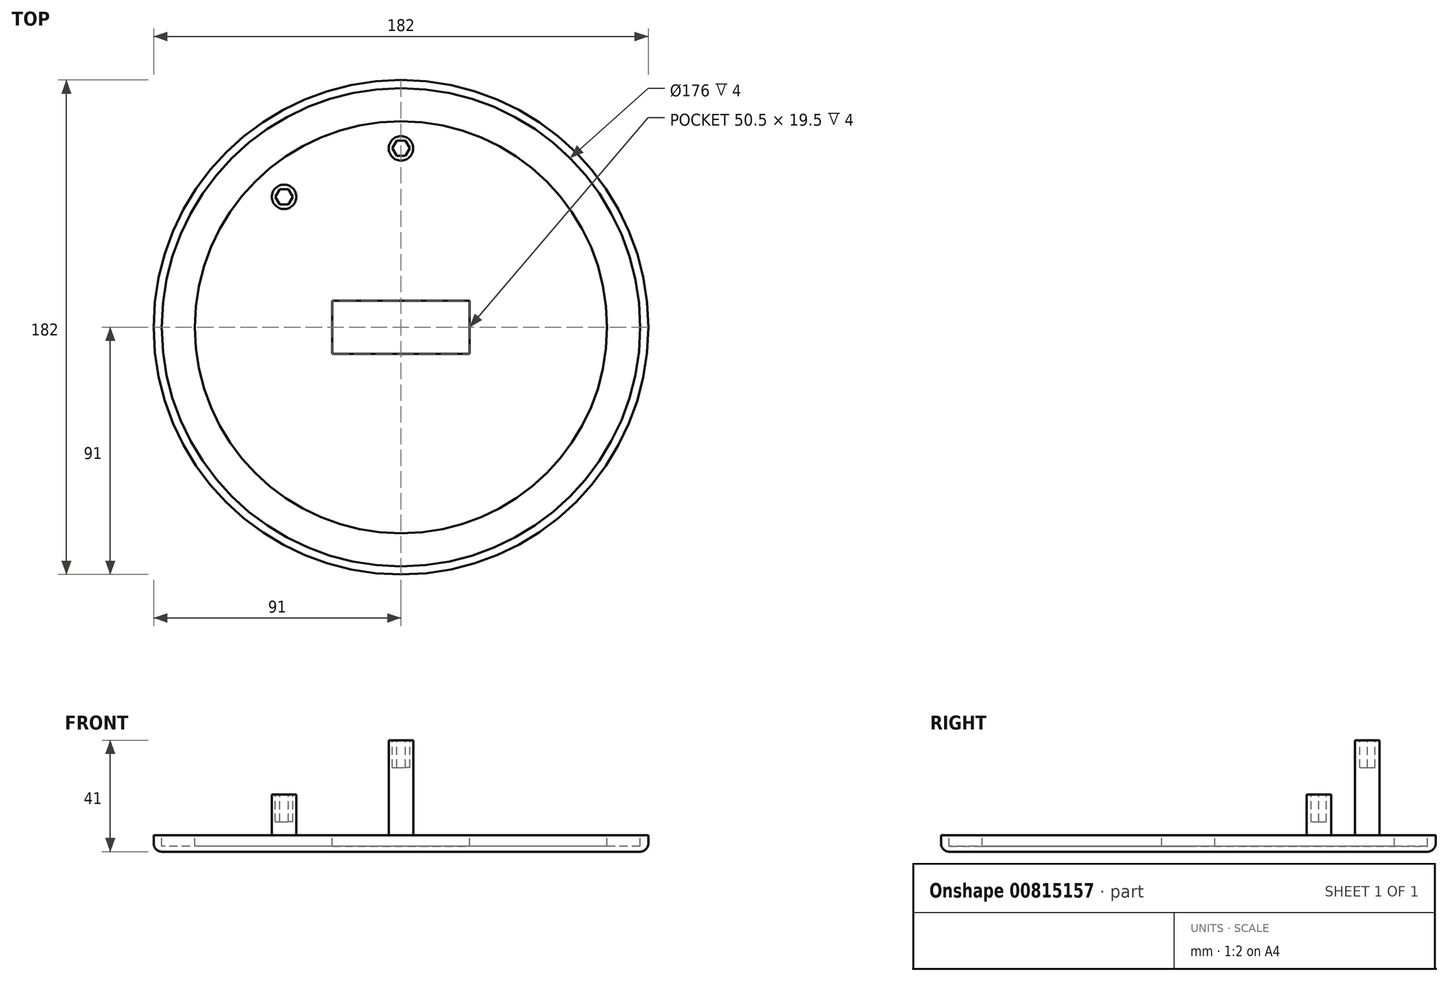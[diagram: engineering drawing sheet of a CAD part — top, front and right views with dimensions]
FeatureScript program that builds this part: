
annotation { "Feature Type Name" : "Feature", "Feature Type Description" : "" }
export const myFeature = defineFeature(function(context is Context, id is Id, definition is map)
    precondition{}
    {
        {
            var Q0;
            Q0=qCreatedBy(makeId("Top.planeOp"),FACE);
            var sketch = newSketch(context, id + "F0", { "sketchPlane" : qUnion([Q0])});
            skCircle(sketch, "E0", {"center": v(0, 0) * mm, "radius": 91 * mm});
            skSolve(sketch);
        }
        {
            var Q0;
            Q0=makeQuery(id+"F0.imprint","IMPRINT",FACE,{"disambiguationData":[TD([[makeQuery(id+"F0.imprint","IMPRINT",EDGE,{"derivedFrom":sQuery(id+"F0.wireOp",EDGE,"E0")}),1.0]])]});
            var Q1;
            Q1=sQuery(id+"F0.wireOp",EDGE,"E0");
            extrude(context, id + "F1", {"entities" : qUnion([Q0]), "surfaceEntities" : qUnion([Q1]), "depth" : 6 * mm, "offsetDistance" : 25 * mm});
        }
        {
            var Q0;
            Q0=makeQuery(id+"F1.opExtrude","CAP_FACE",FACE,{"disambiguationData":[OSD([sQuery(id+"F0.wireOp",EDGE,"E0")])],"isStart":false});
            var sketch = newSketch(context, id + "F2", { "sketchPlane" : qUnion([Q0])});
            skCircle(sketch, "E1", {"center": v(0, 0) * mm, "radius": 88 * mm});
            skSolve(sketch);
        }
        {
            var Q0;
            Q0=makeQuery(id+"F2.imprint","IMPRINT",FACE,{"disambiguationData":[TD([[makeQuery(id+"F2.imprint","IMPRINT",EDGE,{"derivedFrom":sQuery(id+"F2.wireOp",EDGE,"E1")}),-1.0]])]});
            var sketch = newSketch(context, id + "F3", { "sketchPlane" : qUnion([Q0])});
            skCircle(sketch, "E2", {"center": v(0, 0) * mm, "radius": 75.85 * mm});
            skSolve(sketch);
        }
        {
            var Q0;
            Q0=makeQuery(id+"F3.imprint","IMPRINT",FACE,{"disambiguationData":[TD([[makeQuery(id+"F3.imprint","IMPRINT",EDGE,{"derivedFrom":sQuery(id+"F3.wireOp",EDGE,"E2")}),-1.0]])]});
            var Q1;
            Q1=sQuery(id+"F2.wireOp",EDGE,"E1");
            var Q2;
            Q2=sQuery(id+"F3.wireOp",EDGE,"E2");
            extrude(context, id + "F4", {"entities" : qUnion([Q0]), "operationType" : NewBodyOperationType.REMOVE, "surfaceEntities" : qUnion([Q1, Q2]), "oppositeDirection" : true, "depth" : 4 * mm, "offsetDistance" : 25 * mm});
        }
        {
            var Q0;
            Q0=makeQuery(id+"F4.boolean.opBoolean","SPLIT",FACE,{"disambiguationData":[TD([makeQuery(id+"F4.opExtrude","SWEPT_FACE",FACE,{"disambiguationData":[OSD([sQuery(id+"F3.wireOp",EDGE,"E2")])]})])],"derivedFrom":makeQuery(id+"F1.opExtrude","CAP_FACE",FACE,{"disambiguationData":[OSD([sQuery(id+"F0.wireOp",EDGE,"E0")])],"isStart":false})});
            var sketch = newSketch(context, id + "F5", { "sketchPlane" : qUnion([Q0])});
            skLineSegment(sketch, "E3.bottom", {"start": v(-25.25, 9.75) * mm, "end": v(25.25, 9.75) * mm});
            skLineSegment(sketch, "E3.top", {"start": v(-25.25, -9.75) * mm, "end": v(25.25, -9.75) * mm});
            skLineSegment(sketch, "E3.left", {"start": v(-25.25, 9.75) * mm, "end": v(-25.25, -9.75) * mm});
            skLineSegment(sketch, "E3.right", {"start": v(25.25, 9.75) * mm, "end": v(25.25, -9.75) * mm});
            skPoint(sketch, "E3.middle", {"position": v(0, 0) * mm});
            skSolve(sketch);
        }
        {
            var Q0;
            Q0=qSketchRegion(id+"F5",true);
            extrude(context, id + "F6", {"entities" : qUnion([Q0]), "operationType" : NewBodyOperationType.REMOVE, "oppositeDirection" : true, "depth" : 4 * mm, "offsetDistance" : 25 * mm});
        }
        {
            var Q0;
            Q0=makeQuery(id+"FstaHTkGCtETjQ8_1.boolean.opBoolean","SPLIT",FACE,{"disambiguationData":[TD([makeQuery(id+"F6.boolean.opBoolean","COPY",FACE,{"derivedFrom":makeQuery(id+"F6.opExtrude","SWEPT_FACE",FACE,{"disambiguationData":[OSD([sQuery(id+"F5.wireOp",EDGE,"E3.bottom")])]})})])],"derivedFrom":makeQuery(id+"F4.boolean.opBoolean","SPLIT",FACE,{"disambiguationData":[TD([makeQuery(id+"F4.opExtrude","SWEPT_FACE",FACE,{"disambiguationData":[OSD([sQuery(id+"F3.wireOp",EDGE,"E2")])]})])],"derivedFrom":makeQuery(id+"F1.opExtrude","CAP_FACE",FACE,{"disambiguationData":[OSD([sQuery(id+"F0.wireOp",EDGE,"E0")])],"isStart":false})})});
            var sketch = newSketch(context, id + "F7", { "sketchPlane" : qUnion([Q0])});
            skLineSegment(sketch, "E4.bottom", {"start": v(-48, 53) * mm, "end": v(48, 53) * mm});
            skLineSegment(sketch, "E4.top", {"start": v(-48, -53) * mm, "end": v(48, -53) * mm});
            skLineSegment(sketch, "E4.left", {"start": v(-48, 53) * mm, "end": v(-48, -53) * mm});
            skLineSegment(sketch, "E4.right", {"start": v(48, 53) * mm, "end": v(48, -53) * mm});
            skPoint(sketch, "E4.middle", {"position": v(0, 0) * mm});
            skSolve(sketch);
        }
        {
            var Q0;
            Q0=makeQuery(id+"F7.imprint","IMPRINT",FACE,{"disambiguationData":[TD([[makeQuery(id+"F7.imprint","IMPRINT",EDGE,{"derivedFrom":sQuery(id+"F7.wireOp",EDGE,"E4.bottom")}),1.0]])]});
            var sketch = newSketch(context, id + "F8", { "sketchPlane" : qUnion([Q0])});
            skCircle(sketch, "E5", {"center": v(0, 65.85) * mm, "radius": 4.5 * mm});
            skSolve(sketch);
        }
        {
            var Q0;
            Q0=qSketchRegion(id+"F8",true);
            extrude(context, id + "F9", {"entities" : qUnion([Q0]), "operationType" : NewBodyOperationType.ADD, "depth" : 35 * mm, "offsetDistance" : 25 * mm});
        }
        {
            var Q0;
            Q0=makeQuery(id+"F9.opExtrude","CAP_FACE",FACE,{"disambiguationData":[OSD([sQuery(id+"F8.wireOp",EDGE,"E5")])],"isStart":false});
            var sketch = newSketch(context, id + "F10", { "sketchPlane" : qUnion([Q0])});
            skCircle(sketch, "E6.cCircle", {"center": v(0, 65.85) * mm, "radius": 3.23 * mm, "construction": true});
            skLineSegment(sketch, "E6.0", {"start": v(-1.62, 68.65) * mm, "end": v(1.62, 68.65) * mm});
            skLineSegment(sketch, "E6.1", {"start": v(1.62, 68.65) * mm, "end": v(3.23, 65.85) * mm});
            skLineSegment(sketch, "E6.2", {"start": v(3.23, 65.85) * mm, "end": v(1.62, 63.05) * mm});
            skLineSegment(sketch, "E6.3", {"start": v(1.62, 63.05) * mm, "end": v(-1.62, 63.05) * mm});
            skLineSegment(sketch, "E6.4", {"start": v(-1.62, 63.05) * mm, "end": v(-3.23, 65.85) * mm});
            skLineSegment(sketch, "E6.5", {"start": v(-3.23, 65.85) * mm, "end": v(-1.62, 68.65) * mm});
            skSolve(sketch);
        }
        {
            var Q0;
            Q0=makeQuery(id+"F10.imprint","IMPRINT",FACE,{"disambiguationData":[TD([[makeQuery(id+"F10.imprint","IMPRINT",EDGE,{"derivedFrom":sQuery(id+"F10.wireOp",EDGE,"E6.0")}),-1.0]])]});
            extrude(context, id + "F11", {"entities" : qUnion([Q0]), "operationType" : NewBodyOperationType.REMOVE, "oppositeDirection" : true, "depth" : 10 * mm, "offsetDistance" : 25 * mm});
        }
        {
            var Q0;
            Q0=makeQuery(id+"F7.imprint","IMPRINT",FACE,{"disambiguationData":[TD([[makeQuery(id+"F7.imprint","IMPRINT",EDGE,{"derivedFrom":sQuery(id+"F7.wireOp",EDGE,"E4.bottom")}),-1.0]])]});
            var sketch = newSketch(context, id + "F12", { "sketchPlane" : qUnion([Q0])});
            skCircle(sketch, "E7", {"center": v(-43, 48) * mm, "radius": 4.5 * mm});
            skSolve(sketch);
        }
        {
            var Q0;
            Q0=qSketchRegion(id+"F12",true);
            extrude(context, id + "F13", {"entities" : qUnion([Q0]), "operationType" : NewBodyOperationType.ADD, "depth" : 15 * mm, "offsetDistance" : 25 * mm});
        }
        {
            var Q0;
            Q0=makeQuery(id+"F13.opExtrude","CAP_FACE",FACE,{"disambiguationData":[OSD([sQuery(id+"F12.wireOp",EDGE,"E7")])],"isStart":false});
            var sketch = newSketch(context, id + "F14", { "sketchPlane" : qUnion([Q0])});
            skCircle(sketch, "E8.cCircle", {"center": v(-43, 48) * mm, "radius": 3.23 * mm, "construction": true});
            skLineSegment(sketch, "E8.0", {"start": v(-44.62, 50.8) * mm, "end": v(-41.38, 50.8) * mm});
            skLineSegment(sketch, "E8.1", {"start": v(-41.38, 50.8) * mm, "end": v(-39.77, 48) * mm});
            skLineSegment(sketch, "E8.2", {"start": v(-39.77, 48) * mm, "end": v(-41.38, 45.2) * mm});
            skLineSegment(sketch, "E8.3", {"start": v(-41.38, 45.2) * mm, "end": v(-44.62, 45.2) * mm});
            skLineSegment(sketch, "E8.4", {"start": v(-44.62, 45.2) * mm, "end": v(-46.23, 48) * mm});
            skLineSegment(sketch, "E8.5", {"start": v(-46.23, 48) * mm, "end": v(-44.62, 50.8) * mm});
            skSolve(sketch);
        }
        {
            var Q0;
            Q0=qSketchRegion(id+"F14",true);
            extrude(context, id + "F15", {"entities" : qUnion([Q0]), "operationType" : NewBodyOperationType.REMOVE, "oppositeDirection" : true, "depth" : 10 * mm, "offsetDistance" : 25 * mm});
        }
        {
            var Q0;
            Q0=makeQuery(id+"F1.opExtrude","CAP_EDGE",EDGE,{"disambiguationData":[OSD([sQuery(id+"F0.wireOp",EDGE,"E0")])],"isStart":true});
            fillet(context, id + "F16", {"entities" : qUnion([Q0]), "radius" : 3 * mm, "tangentPropagation" : true, "allowEdgeOverflow" : false});
        }
    });
